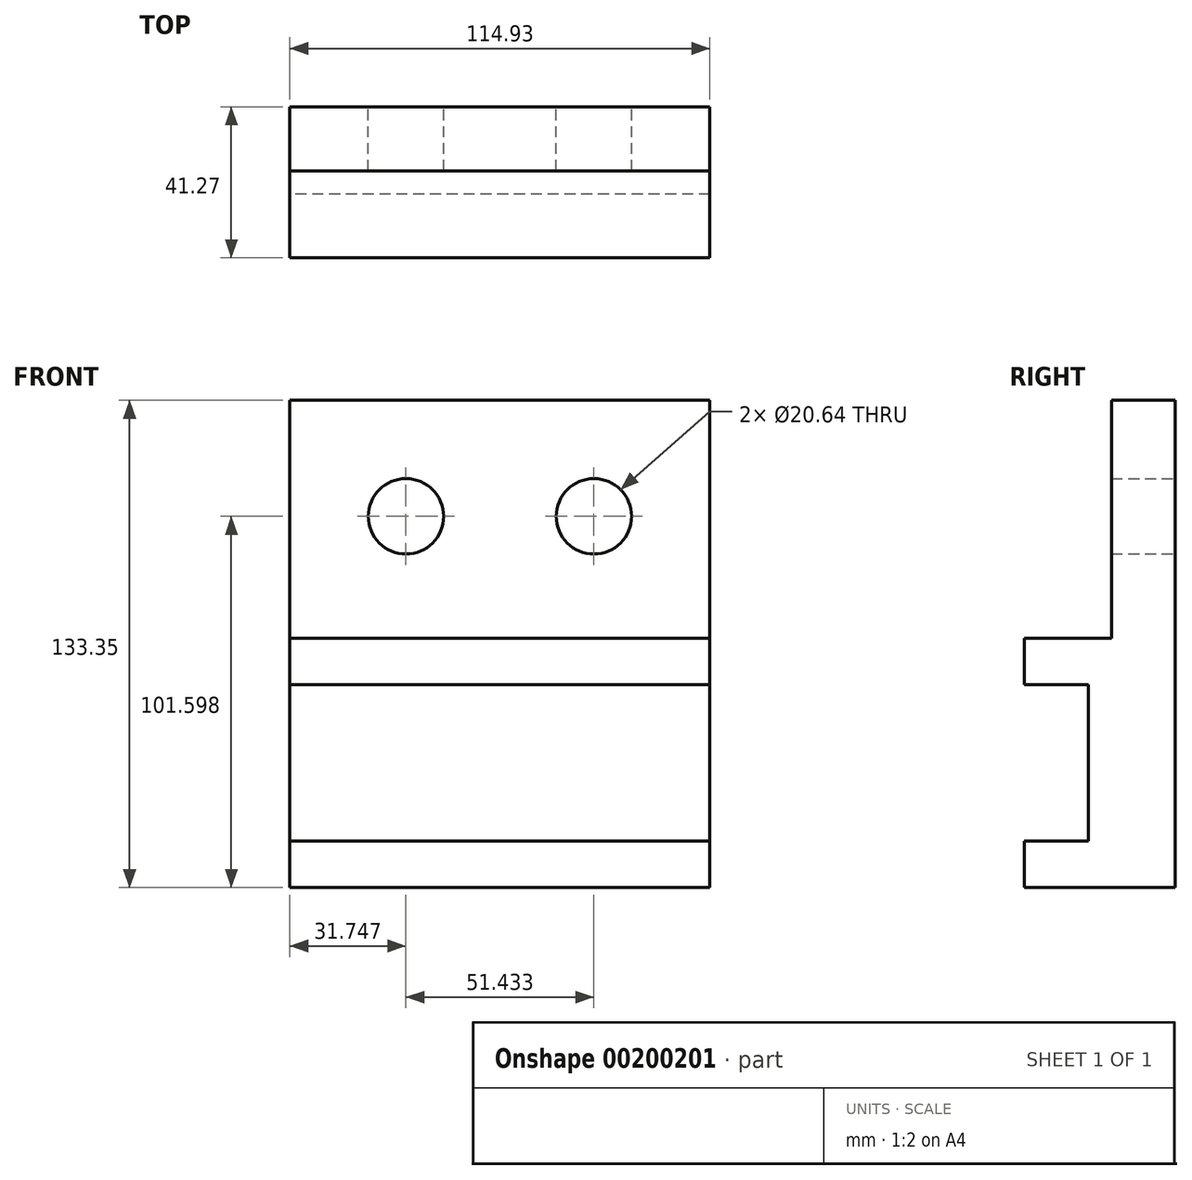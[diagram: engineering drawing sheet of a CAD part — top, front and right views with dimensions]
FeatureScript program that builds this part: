
annotation { "Feature Type Name" : "Feature", "Feature Type Description" : "" }
export const myFeature = defineFeature(function(context is Context, id is Id, definition is map)
    precondition{}
    {
        {
            var Q0;
            Q0=qCreatedBy(makeId("Front.planeOp"),FACE);
            var sketch = newSketch(context, id + "F0", { "sketchPlane" : qUnion([Q0])});
            skLineSegment(sketch, "E0.bottom", {"start": v(-67.72, 65.87) * mm, "end": v(47.21, 65.87) * mm});
            skLineSegment(sketch, "E0.top", {"start": v(-67.72, -67.48) * mm, "end": v(47.21, -67.48) * mm});
            skLineSegment(sketch, "E0.left", {"start": v(-67.72, 65.87) * mm, "end": v(-67.72, -67.48) * mm});
            skLineSegment(sketch, "E0.right", {"start": v(47.21, 65.87) * mm, "end": v(47.21, -67.48) * mm});
            skLineSegment(sketch, "E1", {"start": v(-67.72, 65.87) * mm, "end": v(-67.72, 0.78) * mm});
            skLineSegment(sketch, "E2", {"start": v(-67.72, 0.78) * mm, "end": v(47.21, 0.78) * mm});
            skCircle(sketch, "E3", {"center": v(-35.97, 34.12) * mm, "radius": 10.32 * mm});
            skCircle(sketch, "E4", {"center": v(15.46, 34.12) * mm, "radius": 10.32 * mm});
            skLineSegment(sketch, "E5", {"start": v(-67.72, -54.78) * mm, "end": v(47.21, -54.78) * mm});
            skLineSegment(sketch, "E6", {"start": v(-67.72, -11.92) * mm, "end": v(47.21, -11.92) * mm});
            skSolve(sketch);
        }
        {
            var Q0;
            Q0 = qSketchRegion(id + "F0", true);
            extrude(context, id + "F1", {"entities" : qUnion([Q0]), "depth" : 17.46 * mm});
        }
        {
            var Q0;
            {var subQ0=sQuery(id+"F0.wireOp",EDGE,"E0.top");Q0=makeQuery(id+"F0.imprint","IMPRINT",FACE,{"disambiguationData":[TD([[makeQuery(id+"F0.imprint","IMPRINT",EDGE,{"derivedFrom":subQ0}),1.0]])]});}
            var Q1;
            {var subQ0=sQuery(id+"F0.wireOp",EDGE,"E5");Q1=makeQuery(id+"F0.imprint","IMPRINT",FACE,{"disambiguationData":[TD([[makeQuery(id+"F0.imprint","IMPRINT",EDGE,{"derivedFrom":subQ0}),1.0]])]});}
            var Q2;
            {var subQ0=sQuery(id+"F0.wireOp",EDGE,"E2");Q2=makeQuery(id+"F0.imprint","IMPRINT",FACE,{"disambiguationData":[TD([[makeQuery(id+"F0.imprint","IMPRINT",EDGE,{"derivedFrom":subQ0}),-1.0]])]});}
            extrude(context, id + "F2", {"entities" : qUnion([Q0, Q1, Q2]), "operationType" : NewBodyOperationType.ADD, "depth" : 23.8 * mm});
        }
        {
            var Q0;
            {var subQ0=sQuery(id+"F0.wireOp",EDGE,"E2");Q0=makeQuery(id+"F0.imprint","IMPRINT",FACE,{"disambiguationData":[TD([[makeQuery(id+"F0.imprint","IMPRINT",EDGE,{"derivedFrom":subQ0}),-1.0]])]});}
            var Q1;
            {var subQ0=sQuery(id+"F0.wireOp",EDGE,"E0.top");Q1=makeQuery(id+"F0.imprint","IMPRINT",FACE,{"disambiguationData":[TD([[makeQuery(id+"F0.imprint","IMPRINT",EDGE,{"derivedFrom":subQ0}),1.0]])]});}
            extrude(context, id + "F3", {"entities" : qUnion([Q0, Q1]), "operationType" : NewBodyOperationType.ADD, "depth" : 41.27 * mm});
        }
    });
